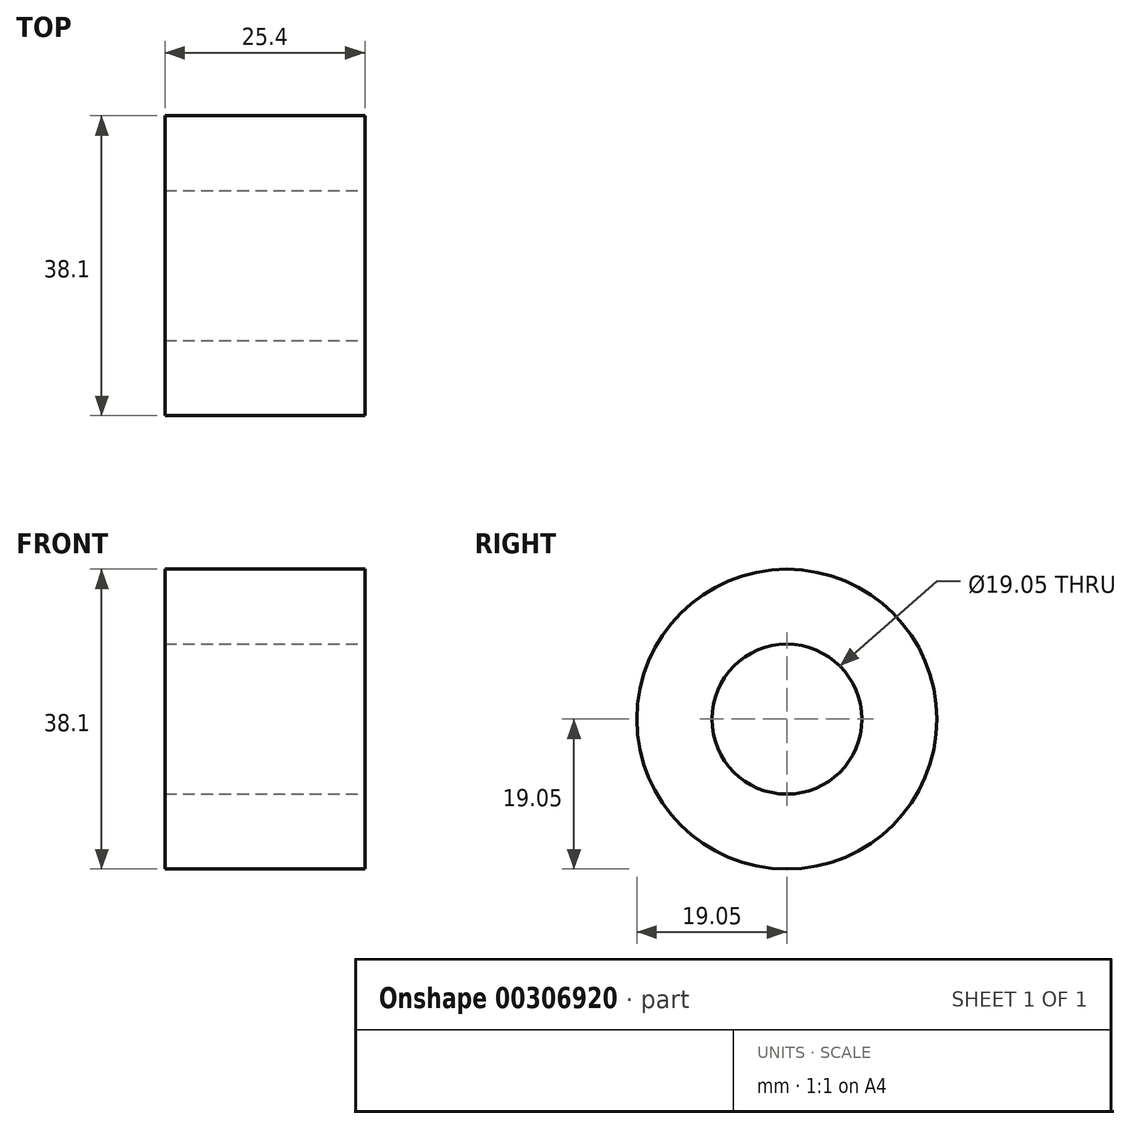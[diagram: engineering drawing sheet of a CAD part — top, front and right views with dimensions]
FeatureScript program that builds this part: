
annotation { "Feature Type Name" : "Feature", "Feature Type Description" : "" }
export const myFeature = defineFeature(function(context is Context, id is Id, definition is map)
    precondition{}
    {
        {
            var Q0;
            Q0=qCreatedBy(makeId("Right.planeOp"),FACE);
            var sketch = newSketch(context, id + "F0", { "sketchPlane" : qUnion([Q0])});
            skCircle(sketch, "E0", {"center": v(0, 0) * mm, "radius": 9.53 * mm});
            skCircle(sketch, "E1", {"center": v(0, 0) * mm, "radius": 19.05 * mm});
            skSolve(sketch);
        }
        {
            var Q0;
            Q0=makeQuery(id+"F0.imprint","IMPRINT",FACE,{"disambiguationData":[TD([[makeQuery(id+"F0.imprint","IMPRINT",EDGE,{"derivedFrom":sQuery(id+"F0.wireOp",EDGE,"E0")}),-1.0]])]});
            extrude(context, id + "F1", {"entities" : qUnion([Q0]), "oppositeDirection" : true, "depth" : 25.4 * mm});
        }
    });
